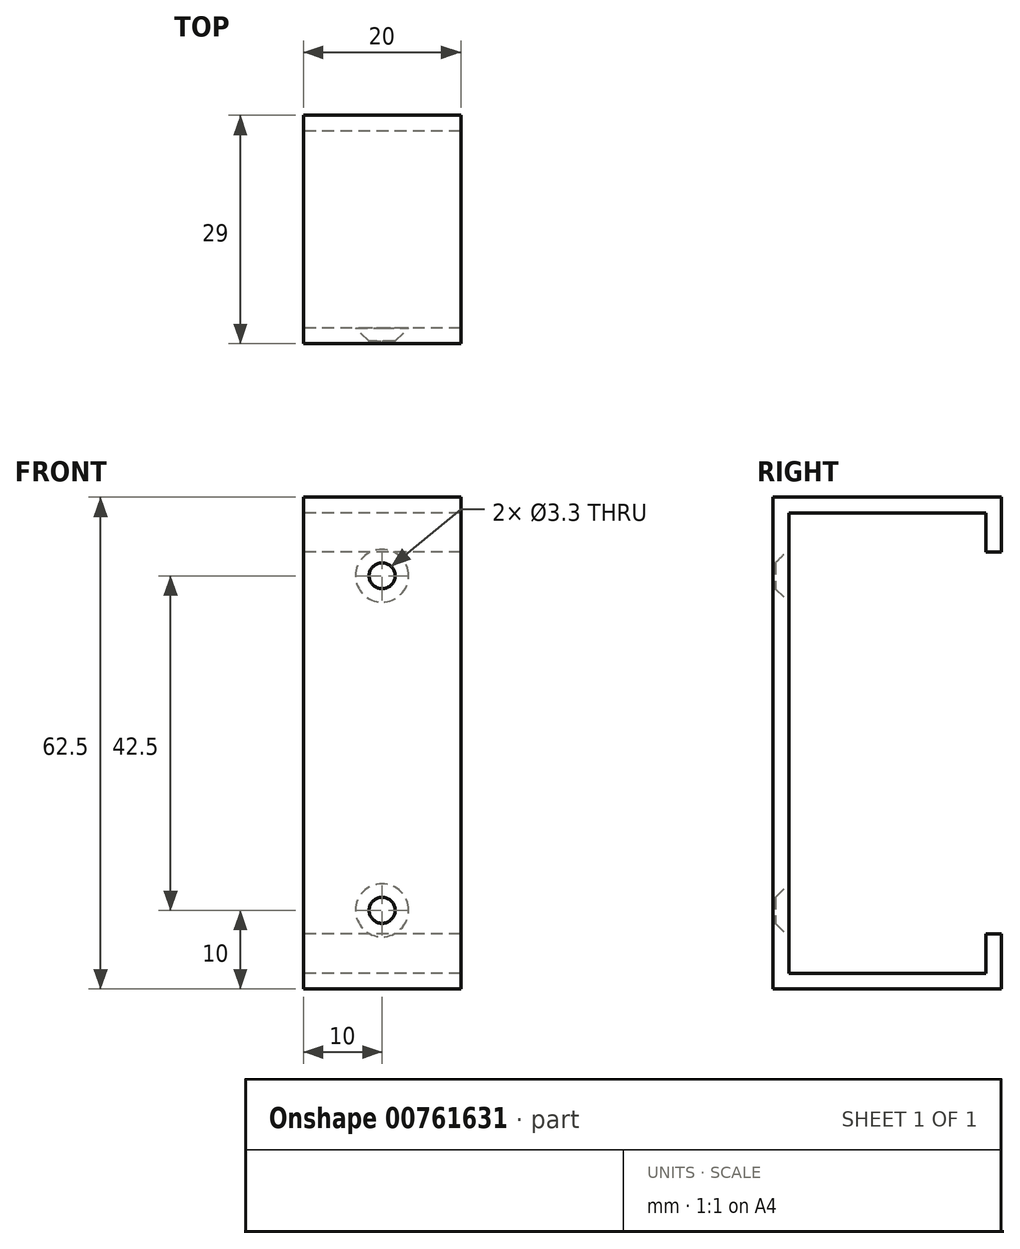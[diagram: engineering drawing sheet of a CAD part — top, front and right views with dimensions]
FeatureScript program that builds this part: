
annotation { "Feature Type Name" : "Feature", "Feature Type Description" : "" }
export const myFeature = defineFeature(function(context is Context, id is Id, definition is map)
    precondition{}
    {
        {
            var Q0;
            Q0=qCreatedBy(makeId("Right.planeOp"),FACE);
            var sketch = newSketch(context, id + "F0", { "sketchPlane" : qUnion([Q0])});
            skLineSegment(sketch, "E0.bottom", {"start": v(14.5, -31.25) * mm, "end": v(-14.5, -31.25) * mm});
            skLineSegment(sketch, "E0.top", {"start": v(14.5, 31.25) * mm, "end": v(-14.5, 31.25) * mm});
            skLineSegment(sketch, "E0.left", {"start": v(14.5, -31.25) * mm, "end": v(14.5, 31.25) * mm});
            skLineSegment(sketch, "E0.right", {"start": v(-14.5, -31.25) * mm, "end": v(-14.5, 31.25) * mm});
            skPoint(sketch, "E0.middle", {"position": v(0, 0) * mm});
            skLineSegment(sketch, "E1.0", {"start": v(12.5, 29.25) * mm, "end": v(-12.5, 29.25) * mm});
            skLineSegment(sketch, "E1.1", {"start": v(12.5, -29.25) * mm, "end": v(12.5, 29.25) * mm});
            skLineSegment(sketch, "E1.2", {"start": v(12.5, -29.25) * mm, "end": v(-12.5, -29.25) * mm});
            skLineSegment(sketch, "E1.3", {"start": v(-12.5, -29.25) * mm, "end": v(-12.5, 29.25) * mm});
            skSolve(sketch);
        }
        {
            var Q0;
            Q0=makeQuery(id+"F0.imprint","IMPRINT",FACE,{"disambiguationData":[TD([[makeQuery(id+"F0.imprint","IMPRINT",EDGE,{"derivedFrom":sQuery(id+"F0.wireOp",EDGE,"E0.bottom")}),-1.0]])]});
            extrude(context, id + "F1", {"entities" : qUnion([Q0]), "depth" : 20 * mm, "offsetDistance" : 25 * mm});
        }
        {
            var Q0;
            Q0=makeQuery(id+"F1.opExtrude","SWEPT_FACE",FACE,{"disambiguationData":[OSD([sQuery(id+"F0.wireOp",EDGE,"E0.left")])]});
            var sketch = newSketch(context, id + "F2", { "sketchPlane" : qUnion([Q0])});
            skLineSegment(sketch, "E2.bottom", {"start": v(-20, 26.25) * mm, "end": v(0, 26.25) * mm});
            skLineSegment(sketch, "E2.top", {"start": v(-20, -26.25) * mm, "end": v(0, -26.25) * mm});
            skLineSegment(sketch, "E2.left", {"start": v(-20, 26.25) * mm, "end": v(-20, -26.25) * mm});
            skLineSegment(sketch, "E2.right", {"start": v(0, 26.25) * mm, "end": v(0, -26.25) * mm});
            skSolve(sketch);
        }
        {
            var Q0;
            Q0=makeQuery(id+"F2.imprint","IMPRINT",FACE,{"disambiguationData":[TD([[makeQuery(id+"F2.imprint","IMPRINT",EDGE,{"derivedFrom":sQuery(id+"F2.wireOp",EDGE,"E2.bottom")}),-1.0]])]});
            extrude(context, id + "F3", {"entities" : qUnion([Q0]), "operationType" : NewBodyOperationType.REMOVE, "oppositeDirection" : true, "depth" : 2 * mm, "offsetDistance" : 25 * mm});
        }
        {
            var Q0;
            Q0=makeQuery(id+"F1.opExtrude","SWEPT_FACE",FACE,{"disambiguationData":[OSD([sQuery(id+"F0.wireOp",EDGE,"E1.3")])]});
            var sketch = newSketch(context, id + "F4", { "sketchPlane" : qUnion([Q0])});
            skLineSegment(sketch, "E3", {"start": v(-10, 28.15) * mm, "end": v(-10, -27.84) * mm, "construction": true});
            skPoint(sketch, "E3.startSnap0", {"position": v(-10, 29.25) * mm});
            skPoint(sketch, "E4", {"position": v(-10, 21.25) * mm});
            skPoint(sketch, "E5", {"position": v(-10, -21.25) * mm});
            skSolve(sketch);
        }
        {
            var Q0;
            Q0=sQuery(id+"F4.wireOp",VERTEX,"E4");
            var Q1;
            Q1=sQuery(id+"F4.wireOp",VERTEX,"E5");
            var Q2;
            Q2=makeQuery(id+"F1.opExtrude","SWEPT_BODY",BODY,{"disambiguationData":[OSD([sQuery(id+"F0.wireOp",EDGE,"E0.bottom"),sQuery(id+"F0.wireOp",EDGE,"E0.top"),sQuery(id+"F0.wireOp",EDGE,"E0.left"),sQuery(id+"F0.wireOp",EDGE,"E0.right"),sQuery(id+"F0.wireOp",EDGE,"E1.0"),sQuery(id+"F0.wireOp",EDGE,"E1.1"),sQuery(id+"F0.wireOp",EDGE,"E1.2"),sQuery(id+"F0.wireOp",EDGE,"E1.3")])]});
            hole(context, id + "F5", {"style" : HoleStyle.C_SINK, "endStyle" : HoleEndStyle.THROUGH, "standardTappedOrClearance" : lookupTablePath({ "standard" : "ISO", "fit" : "Normal", "size" : "M3", "type" : "Clearance" }), "standardBlindInLast" : lookupTablePath({ "fit" : "Standard", "standard" : "ISO", "size" : "M3", "type" : "Clearance" }), "holeDiameter" : 3.3 * mm, "cSinkDiameter" : 6.72 * mm, "cSinkAngle" : 90 * degree, "majorDiameter" : 5 * mm, "isTappedThrough" : true, "tappedDepth" : 12 * mm, "tapClearance" : 3, "locations" : qUnion([Q0, Q1]), "scope" : qUnion([Q2])});
        }
        {
            var Q0;
            Q0=makeQuery(id+"F3.boolean.opBoolean","COPY",FACE,{"derivedFrom":makeQuery(id+"F3.opExtrude","SWEPT_FACE",FACE,{"disambiguationData":[OSD([sQuery(id+"F2.wireOp",EDGE,"E2.bottom")])]})});
            extrude(context, id + "F6", {"entities" : qUnion([Q0]), "operationType" : NewBodyOperationType.ADD, "depth" : 2 * mm, "offsetDistance" : 25 * mm});
        }
        {
            var Q0;
            Q0=makeQuery(id+"F3.boolean.opBoolean","COPY",FACE,{"derivedFrom":makeQuery(id+"F3.opExtrude","SWEPT_FACE",FACE,{"disambiguationData":[OSD([sQuery(id+"F2.wireOp",EDGE,"E2.top")])]})});
            extrude(context, id + "F7", {"entities" : qUnion([Q0]), "operationType" : NewBodyOperationType.ADD, "depth" : 2 * mm, "offsetDistance" : 25 * mm});
        }
    });
